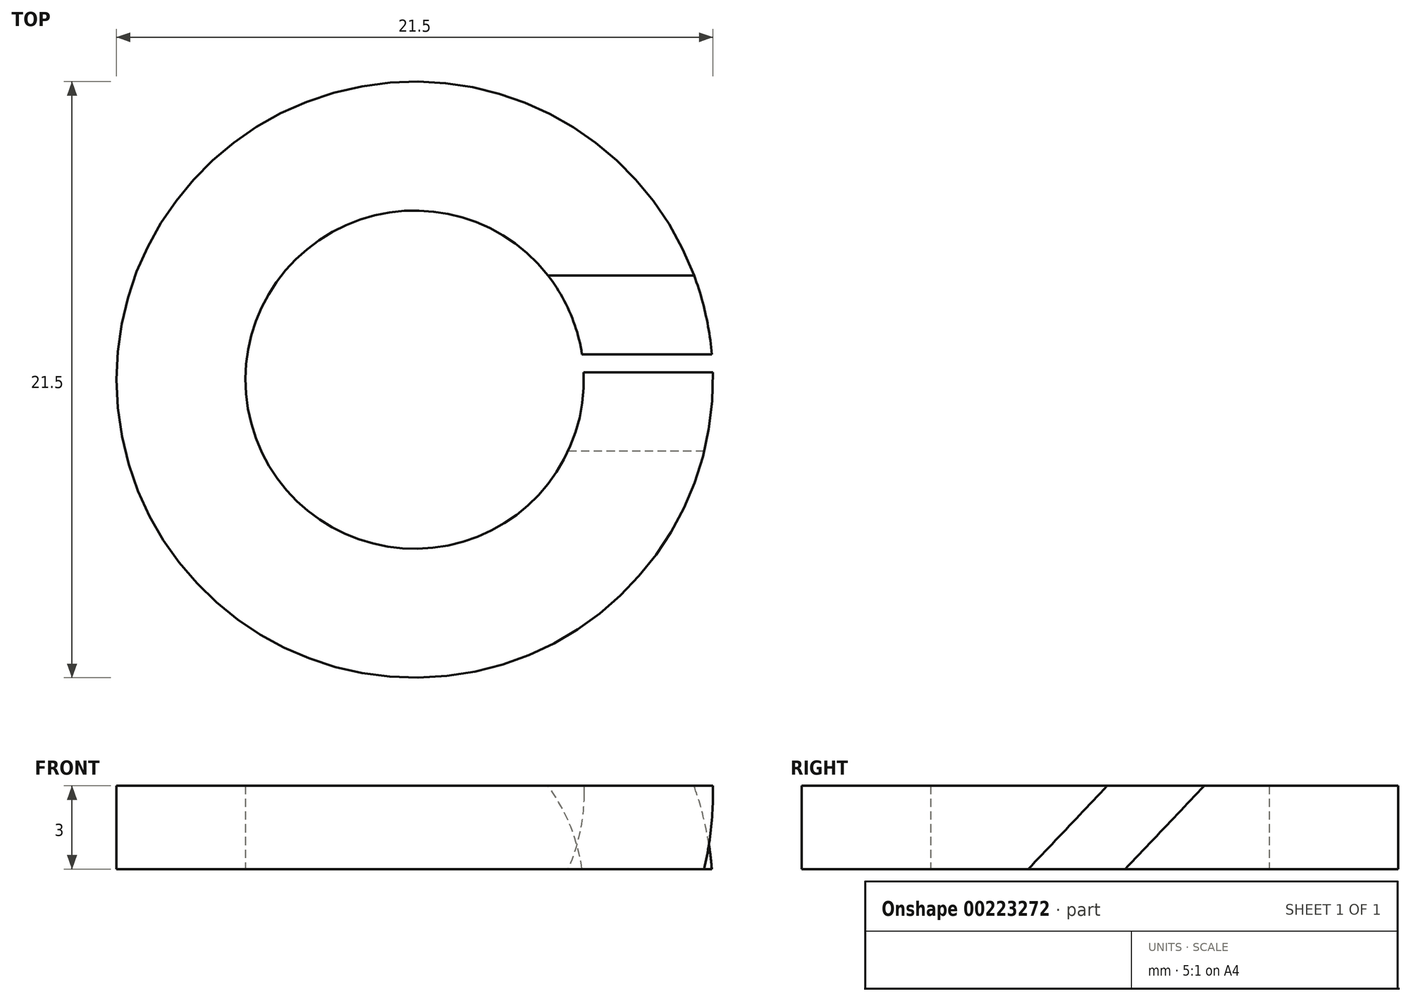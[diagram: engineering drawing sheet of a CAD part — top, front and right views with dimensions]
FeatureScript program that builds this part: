
annotation { "Feature Type Name" : "Feature", "Feature Type Description" : "" }
export const myFeature = defineFeature(function(context is Context, id is Id, definition is map)
    precondition{}
    {
        {
            var Q0;
            Q0=qCreatedBy(makeId("Top.planeOp"),FACE);
            var sketch = newSketch(context, id + "F0", { "sketchPlane" : qUnion([Q0])});
            skCircle(sketch, "E0", {"center": v(0, 0) * mm, "radius": 10.75 * mm});
            skCircle(sketch, "E1", {"center": v(0, 0) * mm, "radius": 6.1 * mm});
            skSolve(sketch);
        }
        {
            var Q0;
            Q0 = qSketchRegion(id + "F0", true);
            extrude(context, id + "F1", {"entities" : qUnion([Q0]), "depth" : 3 * mm});
        }
        {
            var Q0;
            Q0=qCreatedBy(makeId("Right.planeOp"),FACE);
            var sketch = newSketch(context, id + "F2", { "sketchPlane" : qUnion([Q0])});
            skLineSegment(sketch, "E2", {"start": v(1.4, 4.2) * mm, "end": v(-3.5, -0.96) * mm});
            skLineSegment(sketch, "E3", {"start": v(-3.5, -0.96) * mm, "end": v(0, -0.96) * mm});
            skLineSegment(sketch, "E4", {"start": v(0, -0.96) * mm, "end": v(4.2, 3.46) * mm});
            skLineSegment(sketch, "E5", {"start": v(4.2, 3.46) * mm, "end": v(1.4, 4.2) * mm});
            skSolve(sketch);
        }
        {
            var Q0;
            Q0 = qSketchRegion(id + "F2", true);
            extrude(context, id + "F3", {"entities" : qUnion([Q0]), "operationType" : NewBodyOperationType.REMOVE, "depth" : 25 * mm});
        }
    });
